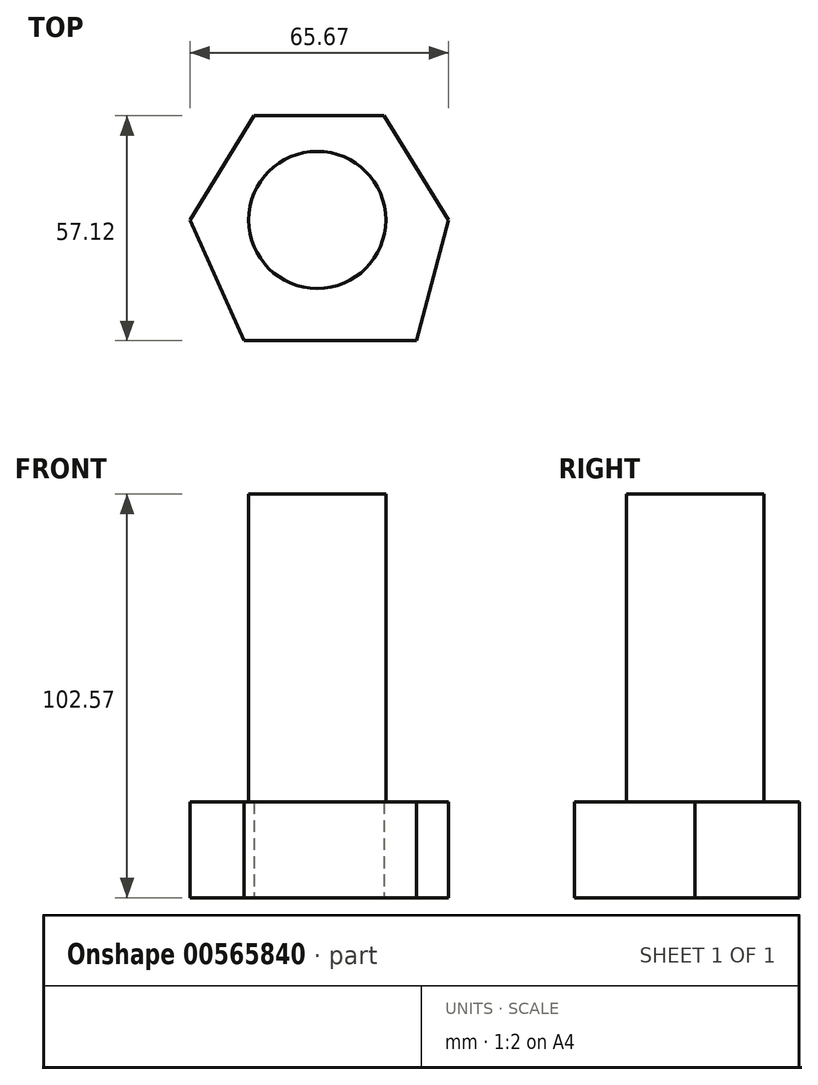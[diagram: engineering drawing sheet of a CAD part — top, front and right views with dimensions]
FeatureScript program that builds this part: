
annotation { "Feature Type Name" : "Feature", "Feature Type Description" : "" }
export const myFeature = defineFeature(function(context is Context, id is Id, definition is map)
    precondition{}
    {
        {
            var Q0;
            Q0=qCreatedBy(makeId("Top.planeOp"),FACE);
            var sketch = newSketch(context, id + "F0", { "sketchPlane" : qUnion([Q0])});
            skLineSegment(sketch, "E0", {"start": v(-32.31, 0) * mm, "end": v(-16.03, 26.47) * mm});
            skLineSegment(sketch, "E1", {"start": v(-16.03, 26.47) * mm, "end": v(17, 26.47) * mm});
            skLineSegment(sketch, "E2", {"start": v(17, 26.47) * mm, "end": v(33.36, 0) * mm});
            skLineSegment(sketch, "E3", {"start": v(33.36, 0) * mm, "end": v(25.18, -30.65) * mm});
            skPoint(sketch, "E3.endSnap0", {"position": v(25.18, 13.23) * mm});
            skLineSegment(sketch, "E4", {"start": v(25.18, -30.65) * mm, "end": v(-18.66, -30.65) * mm});
            skLineSegment(sketch, "E5", {"start": v(-18.66, -30.65) * mm, "end": v(-32.31, 0) * mm});
            skSolve(sketch);
        }
        {
            var Q0;
            Q0=makeQuery(id+"F0.imprint","IMPRINT",FACE,{"disambiguationData":[TD([[makeQuery(id+"F0.imprint","IMPRINT",EDGE,{"derivedFrom":sQuery(id+"F0.wireOp",EDGE,"E0")}),-1.0]])]});
            extrude(context, id + "F1", {"entities" : qUnion([Q0]), "depth" : 24.3 * mm, "offsetDistance" : 25.4 * mm});
        }
        {
            var Q0;
            Q0=qCreatedBy(makeId("Top.planeOp"),FACE);
            var sketch = newSketch(context, id + "F2", { "sketchPlane" : qUnion([Q0])});
            skCircle(sketch, "E6", {"center": v(0, 0) * mm, "radius": 17.42 * mm});
            skSolve(sketch);
        }
        {
            var Q0;
            Q0=makeQuery(id+"F2.imprint","IMPRINT",FACE,{"disambiguationData":[TD([[makeQuery(id+"F2.imprint","IMPRINT",EDGE,{"derivedFrom":sQuery(id+"F2.wireOp",EDGE,"E6")}),1.0]])]});
            extrude(context, id + "F3", {"entities" : qUnion([Q0]), "operationType" : NewBodyOperationType.ADD, "depth" : 102.57 * mm, "offsetDistance" : 25.4 * mm});
        }
    });
